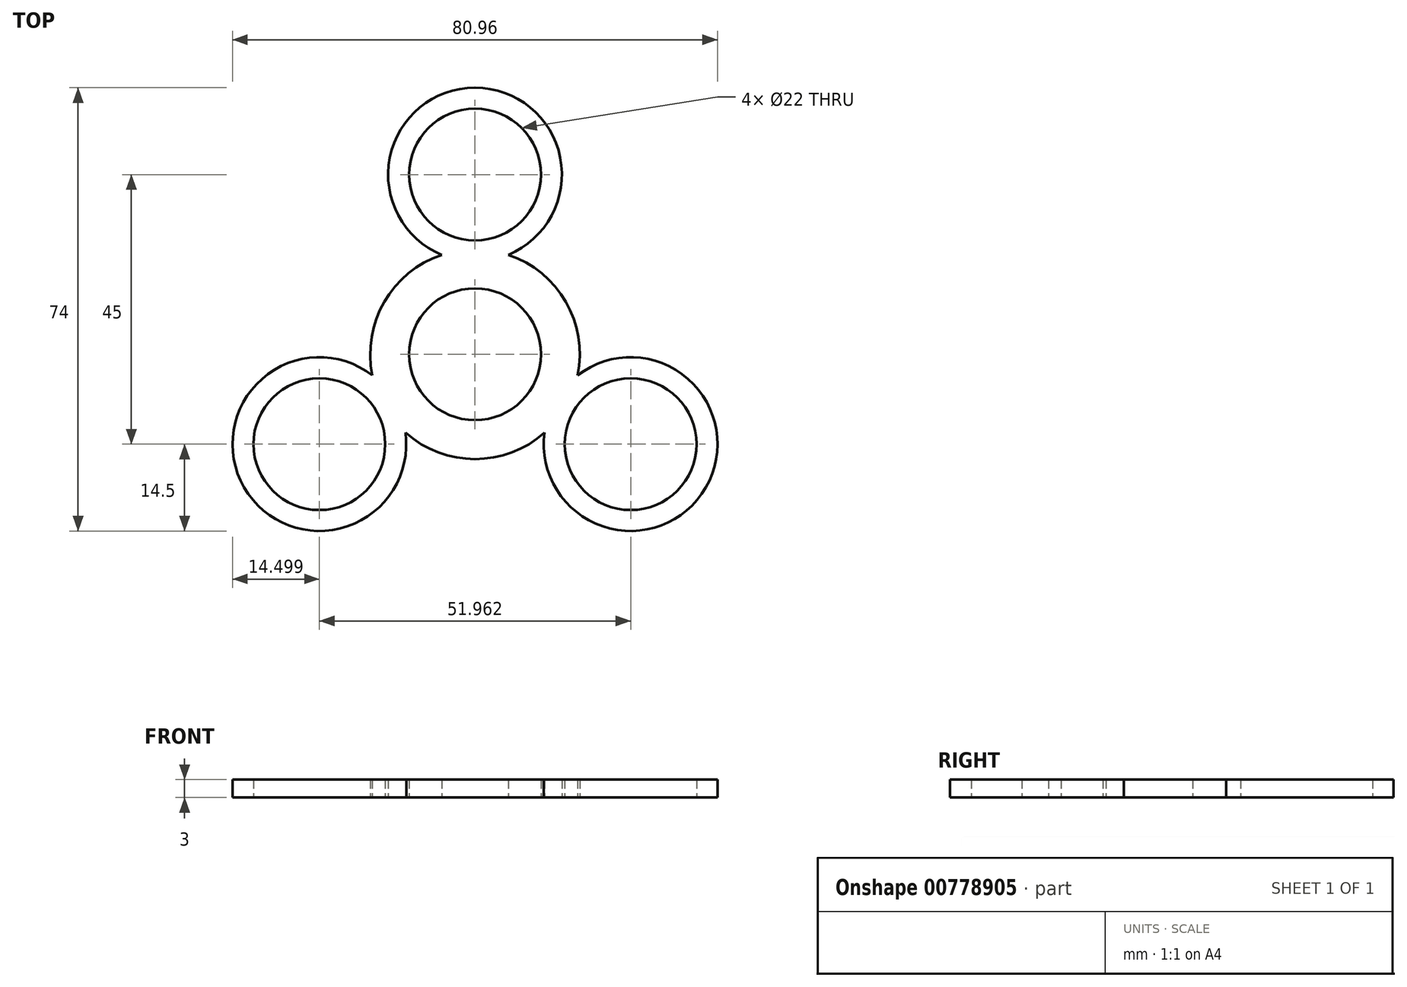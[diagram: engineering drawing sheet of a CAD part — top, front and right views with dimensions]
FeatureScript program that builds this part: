
annotation { "Feature Type Name" : "Feature", "Feature Type Description" : "" }
export const myFeature = defineFeature(function(context is Context, id is Id, definition is map)
    precondition{}
    {
        {
            var Q0;
            Q0=qCreatedBy(makeId("Top.planeOp"),FACE);
            var sketch = newSketch(context, id + "F0", { "sketchPlane" : qUnion([Q0])});
            skCircle(sketch, "E0", {"center": v(0, 30) * mm, "radius": 11 * mm});
            skCircle(sketch, "E1.1.1", {"center": v(0, 0) * mm, "radius": 11 * mm});
            skCircle(sketch, "E1.1.2", {"center": v(-25.98, -15) * mm, "radius": 11 * mm});
            skCircle(sketch, "E1.2.1", {"center": v(0, 0) * mm, "radius": 11 * mm});
            skCircle(sketch, "E1.2.2", {"center": v(25.98, -15) * mm, "radius": 11 * mm});
            skPoint(sketch, "E1.center", {"position": v(0, 0) * mm});
            skArc(sketch, "E2", {"start": v(5.54, 16.6) * mm, "mid": v(0, 44.5) * mm, "end": v(-5.54, 16.6) * mm});
            skArc(sketch, "E3", {"start": v(-5.54, 16.6) * mm, "mid": v(-15.16, 8.75) * mm, "end": v(-17.15, -3.5) * mm});
            skArc(sketch, "E4.1.1", {"start": v(-17.15, -3.5) * mm, "mid": v(-38.54, -22.25) * mm, "end": v(-11.6, -13.1) * mm});
            skArc(sketch, "E4.2.1", {"start": v(11.6, -13.1) * mm, "mid": v(38.54, -22.25) * mm, "end": v(17.15, -3.5) * mm});
            skArc(sketch, "E5.trimOffspring", {"start": v(17.15, -3.5) * mm, "mid": v(15.16, 8.75) * mm, "end": v(5.54, 16.6) * mm});
            skArc(sketch, "E6.trimOffspring", {"start": v(-11.6, -13.1) * mm, "mid": v(0, -17.5) * mm, "end": v(11.6, -13.1) * mm});
            skSolve(sketch);
        }
        {
            var Q0;
            Q0 = qSketchRegion(id + "F0", true);
            extrude(context, id + "F1", {"entities" : qUnion([Q0]), "depth" : 3 * mm, "offsetDistance" : 25 * mm});
        }
    });
